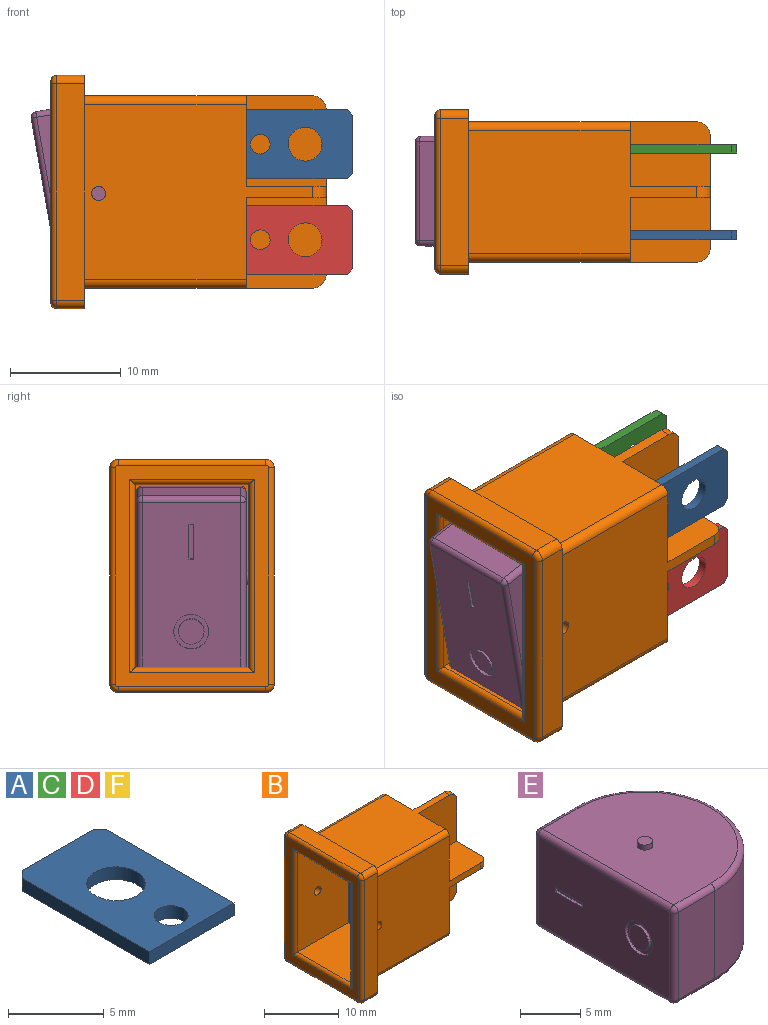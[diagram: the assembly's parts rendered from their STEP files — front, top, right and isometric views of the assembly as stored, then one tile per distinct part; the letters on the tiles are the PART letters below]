
ASSEMBLY  parts=6 mates=5
PART A: 10 faces, bbox 6.2x9.9x0.8 mm
  f0: plane 0.81x0.51mm, normal (0.71,0.7,0), area 0.6mm2, adj f1,f7,f8,f9
  f1: plane 5.25x0.81mm, normal (0,1,0), area 4.3mm2, adj f0,f2,f8,f9
  f2: plane 0.81x0.51mm, normal (-0.71,0.7,0), area 0.6mm2, adj f1,f3,f8,f9
  f3: plane 9.4x0.81mm, normal (-1,0,0), area 7.6mm2, adj f2,f4,f8,f9
  f4: plane 6.25x0.81mm, normal (0,-1,0), area 5.1mm2, adj f3,f7,f8,f9
  f5: cylinder r=1.52mm len=3.05mm, axis (0,0,-1), area 7.8mm2, adj f8,f9
  f6: cylinder r=0.89mm len=1.78mm, axis (0,0,-1), area 4.5mm2, adj f8,f9
  f7: plane 9.4x0.81mm, normal (1,0,0), area 7.6mm2, adj f0,f4,f8,f9
  f8: plane 9.91x6.25mm, normal (0,0,1), area 51.9mm2, adj f0,f1,f2,f3,f4,f5,f6,f7
  f9: plane 9.91x6.25mm, normal (0,0,-1), area 51.9mm2, adj f0,f1,f2,f3,f4,f5,f6,f7
PART B: 74 faces, bbox 24.9x14.9x21.1 mm
  f0: plane 20.07x13.84mm, normal (-1,0,0), area 79.6mm2, adj f58,f59,f60,f61,f62,f63,f64,f65
  f1: plane 8.19x5.84mm, normal (1,0,0), area 42.8mm2, adj f10,f11,f19,f20,f21,f22,f40,f41
  f2: plane 8.19x5.84mm, normal (1,0,0), area 42.8mm2, adj f10,f13,f24,f25,f26,f27,f38,f39
  f3: plane 8.19x5.84mm, normal (1,0,0), area 42.8mm2, adj f12,f13,f29,f30,f31,f32,f36,f37
  f4: plane 8.19x5.84mm, normal (1,0,0), area 42.8mm2, adj f11,f12,f14,f15,f16,f17,f34,f35
  f5: plane 21.08x14.86mm, normal (1,0,0), area 92.3mm2, adj f6,f7,f8,f9,f10,f11,f12,f13
  f6: plane 19.56x2.54mm, normal (0,-1,0), area 49.7mm2, adj f5,f54,f57,f64
  f7: plane 13.34x2.54mm, normal (0,0,-1), area 33.9mm2, adj f5,f54,f55,f63
  f8: plane 19.56x2.54mm, normal (0,1,0), area 49.7mm2, adj f5,f55,f56,f59
  f9: plane 13.34x2.54mm, normal (0,0,1), area 33.9mm2, adj f5,f56,f57,f60
  f10: plane 20.57x15.88mm, normal (0,1,0), area 236.7mm2, adj f1,f2,f5,f39,f40,f48,f50,f53
  f11: plane 20.57x11.18mm, normal (0,0,1), area 169.3mm2, adj f1,f4,f5,f34,f41,f50,f51,f72
  f12: plane 20.57x15.88mm, normal (0,-1,0), area 236.7mm2, adj f3,f4,f5,f35,f36,f49,f51,f52
  f13: plane 20.57x11.18mm, normal (0,0,-1), area 169.3mm2, adj f2,f3,f5,f37,f38,f52,f53,f70
  f14: plane 0.81x0.25mm, normal (0,0,1), area 0.2mm2, adj f4,f15,f17,f18
  f15: plane 6.1x0.25mm, normal (0,-1,0), area 1.5mm2, adj f4,f14,f16,f18
  f16: plane 0.81x0.25mm, normal (0,0,-1), area 0.2mm2, adj f4,f15,f17,f18
  f17: plane 6.1x0.25mm, normal (0,1,0), area 1.5mm2, adj f4,f14,f16,f18
  f18: plane 6.1x0.81mm, normal (1,0,0), area 5mm2, adj f14,f15,f16,f17
  f19: plane 0.81x0.25mm, normal (0,0,1), area 0.2mm2, adj f1,f20,f22,f23
  f20: plane 6.1x0.25mm, normal (0,-1,0), area 1.5mm2, adj f1,f19,f21,f23
  f21: plane 0.81x0.25mm, normal (0,0,-1), area 0.2mm2, adj f1,f20,f22,f23
  f22: plane 6.1x0.25mm, normal (0,1,0), area 1.5mm2, adj f1,f19,f21,f23
  f23: plane 6.1x0.81mm, normal (1,0,0), area 5mm2, adj f19,f20,f21,f22
  f24: plane 0.81x0.25mm, normal (0,0,1), area 0.2mm2, adj f2,f25,f27,f28
  f25: plane 6.1x0.25mm, normal (0,-1,0), area 1.5mm2, adj f2,f24,f26,f28
  f26: plane 0.81x0.25mm, normal (0,0,-1), area 0.2mm2, adj f2,f25,f27,f28
  f27: plane 6.1x0.25mm, normal (0,1,0), area 1.5mm2, adj f2,f24,f26,f28
  f28: plane 6.1x0.81mm, normal (1,0,0), area 5mm2, adj f24,f25,f26,f27
  f29: plane 0.81x0.25mm, normal (0,0,1), area 0.2mm2, adj f3,f30,f32,f33
  f30: plane 6.1x0.25mm, normal (0,-1,0), area 1.5mm2, adj f3,f29,f31,f33
  f31: plane 0.81x0.25mm, normal (0,0,-1), area 0.2mm2, adj f3,f30,f32,f33
  f32: plane 6.1x0.25mm, normal (0,1,0), area 1.5mm2, adj f3,f29,f31,f33
  f33: plane 6.1x0.81mm, normal (1,0,0), area 5mm2, adj f29,f30,f31,f32
  f34: plane 8.19x7.24mm, normal (0,-1,0), area 59mm2, adj f4,f11,f35,f42,f72
  f35: plane 7.24x5.84mm, normal (0,0,1), area 41.9mm2, adj f4,f12,f34,f42,f73
  f36: plane 7.24x5.84mm, normal (0,0,-1), area 41.9mm2, adj f3,f12,f37,f42,f73
  f37: plane 8.19x7.24mm, normal (0,-1,0), area 59mm2, adj f3,f13,f36,f42,f70
  f38: plane 8.19x7.24mm, normal (0,1,0), area 59mm2, adj f2,f13,f39,f42,f70
  f39: plane 7.24x5.84mm, normal (0,0,-1), area 41.9mm2, adj f2,f10,f38,f42,f71
  f40: plane 7.24x5.84mm, normal (0,0,1), area 41.9mm2, adj f1,f10,f41,f42,f71
  f41: plane 8.19x7.24mm, normal (0,1,0), area 59mm2, adj f1,f11,f40,f42,f72
  f42: plane 14.86x10.16mm, normal (1,0,0), area 24.4mm2, adj f34,f35,f36,f37,f38,f39,f40,f41
  f43: plane 16.51x9.65mm, normal (0,1,0), area 158.1mm2, adj f44,f46,f47,f49,f66
  f44: plane 10.29x9.65mm, normal (0,0,-1), area 99.3mm2, adj f43,f45,f47,f67
  f45: plane 16.51x9.65mm, normal (0,-1,0), area 158.1mm2, adj f44,f46,f47,f48,f69
  f46: plane 10.29x9.65mm, normal (0,0,1), area 99.3mm2, adj f43,f45,f47,f68
  f47: plane 16.51x10.29mm, normal (-1,0,0), area 169.8mm2, adj f43,f44,f45,f46
  f48: cylinder r=0.64mm len=1.27mm, axis (0,1,0), area 4.8mm2, adj f10,f45
  f49: cylinder r=0.64mm len=1.27mm, axis (0,1,0), area 4.8mm2, adj f12,f43
  f50: cylinder r=0.76mm len=14.61mm, axis (1,0,0), area 17.5mm2, adj f1,f5,f10,f11
  f51: cylinder r=0.76mm len=14.61mm, axis (-1,0,0), area 17.5mm2, adj f4,f5,f11,f12
  f52: cylinder r=0.76mm len=14.61mm, axis (1,0,0), area 17.5mm2, adj f3,f5,f12,f13
  f53: cylinder r=0.76mm len=14.61mm, axis (-1,0,0), area 17.5mm2, adj f2,f5,f10,f13
  f54: cylinder r=0.76mm len=2.54mm, axis (1,0,0), area 3mm2, adj f5,f6,f7,f65
  f55: cylinder r=0.76mm len=2.54mm, axis (-1,0,0), area 3mm2, adj f5,f7,f8,f61
  f56: cylinder r=0.76mm len=2.54mm, axis (1,0,0), area 3mm2, adj f5,f8,f9,f58
  f57: cylinder r=0.76mm len=2.54mm, axis (-1,0,0), area 3mm2, adj f5,f6,f9,f62
  f58: torus R=0.25mm, axis (1,0,0), area 0.7mm2, adj f0,f56,f59,f60
  f59: cylinder r=0.51mm len=19.56mm, axis (0,0,1), area 15.6mm2, adj f0,f8,f58,f61
  f60: cylinder r=0.51mm len=13.34mm, axis (0,-1,0), area 10.6mm2, adj f0,f9,f58,f62
  f61: torus R=0.25mm, axis (1,0,0), area 0.7mm2, adj f0,f55,f59,f63
  f62: torus R=0.25mm, axis (1,0,0), area 0.7mm2, adj f0,f57,f60,f64
  f63: cylinder r=0.51mm len=13.34mm, axis (0,1,0), area 10.6mm2, adj f0,f7,f61,f65
  f64: cylinder r=0.51mm len=19.56mm, axis (0,0,-1), area 15.6mm2, adj f0,f6,f62,f65
  f65: torus R=0.25mm, axis (1,0,0), area 0.7mm2, adj f0,f54,f63,f64
  f66: cylinder r=0.51mm len=17.53mm, axis (0,0,1), area 13.5mm2, adj f0,f43,f67,f68
  f67: cylinder r=0.51mm len=11.3mm, axis (0,1,0), area 8.5mm2, adj f0,f44,f66,f69
  f68: cylinder r=0.51mm len=11.3mm, axis (0,-1,0), area 8.5mm2, adj f0,f46,f66,f69
  f69: cylinder r=0.51mm len=17.53mm, axis (0,0,-1), area 13.5mm2, adj f0,f45,f67,f68
  f70: cylinder r=1.27mm len=1.27mm, axis (0,-1,0), area 2mm2, adj f13,f37,f38,f42
  f71: cylinder r=1.27mm len=1.27mm, axis (0,0,-1), area 2mm2, adj f10,f39,f40,f42
  f72: cylinder r=1.27mm len=1.27mm, axis (0,1,0), area 2mm2, adj f11,f34,f41,f42
  f73: cylinder r=1.27mm len=1.27mm, axis (0,0,1), area 2mm2, adj f12,f35,f36,f42
PART C: same geometry as A
PART D: same geometry as A
PART E: 33 faces, bbox 13.8x17.9x10.9 mm
  f0: plane 15.49x8.89mm, normal (-1,0,0), area 128.5mm2, adj f11,f14,f15,f16,f17,f22,f24,f27
  f1: cylinder r=8.26mm len=16.51mm, axis (0,0,-1), area 230.6mm2, adj f2,f3,f20,f31
  f2: plane 8.89x4.32mm, normal (0,1,0), area 38.4mm2, adj f1,f19,f24,f29
  f3: plane 8.89x4.32mm, normal (0,-1,0), area 38.4mm2, adj f1,f23,f28,f32
  f4: plane 15.49x12.07mm, normal (0,0,1), area 159.9mm2, adj f6,f19,f20,f22,f23
  f5: plane 15.49x12.07mm, normal (0,0,-1), area 159.9mm2, adj f8,f27,f29,f31,f32
  f6: cylinder r=0.64mm len=1.27mm, axis (0,0,-1), area 2mm2, adj f4,f7
  f7: plane 1.27x1.27mm, normal (0,0,1), area 1.3mm2, adj f6
  f8: cylinder r=0.64mm len=1.27mm, axis (0,0,1), area 2mm2, adj f5,f9
  f9: plane 1.27x1.27mm, normal (0,0,-1), area 1.3mm2, adj f8
  f10: cylinder r=1.16mm len=2.31mm, axis (-1,0,0), area 1.8mm2, adj f12,f13
  f11: cylinder r=1.59mm len=3.18mm, axis (-1,0,0), area 2.5mm2, adj f0,f12
  f12: plane 3.18x3.18mm, normal (-1,0,0), area 3.7mm2, adj f10,f11
  f13: plane 2.31x2.31mm, normal (-1,0,0), area 4.2mm2, adj f10
  f14: plane 3.18x0.25mm, normal (0,0,-1), area 0.8mm2, adj f0,f15,f17,f18
  f15: plane 0.43x0.25mm, normal (0,-1,0), area 0.1mm2, adj f0,f14,f16,f18
  f16: plane 3.18x0.25mm, normal (0,0,1), area 0.8mm2, adj f0,f15,f17,f18
  f17: plane 0.43x0.25mm, normal (0,1,0), area 0.1mm2, adj f0,f14,f16,f18
  f18: plane 3.18x0.43mm, normal (-1,0,0), area 1.4mm2, adj f14,f15,f16,f17
  f19: cylinder r=0.51mm len=4.32mm, axis (1,0,0), area 3.4mm2, adj f2,f4,f20,f21
  f20: torus R=7.75mm, axis (0,0,1), area 20.2mm2, adj f1,f4,f19,f23
  f21: sphere r=0.51mm, area 0.4mm2, adj f19,f22,f24
  f22: cylinder r=0.51mm len=15.49mm, axis (0,1,0), area 12.4mm2, adj f0,f4,f21,f25
  f23: cylinder r=0.51mm len=4.32mm, axis (-1,0,0), area 3.4mm2, adj f3,f4,f20,f25
  f24: cylinder r=0.51mm len=8.89mm, axis (0,0,-1), area 7.1mm2, adj f0,f2,f21,f26
  f25: sphere r=0.51mm, area 0.4mm2, adj f22,f23,f28
  f26: sphere r=0.51mm, area 0.4mm2, adj f24,f27,f29
  f27: cylinder r=0.51mm len=15.49mm, axis (0,-1,0), area 12.4mm2, adj f0,f5,f26,f30
  f28: cylinder r=0.51mm len=8.89mm, axis (0,0,-1), area 7.1mm2, adj f0,f3,f25,f30
  f29: cylinder r=0.51mm len=4.32mm, axis (-1,0,0), area 3.4mm2, adj f2,f5,f26,f31
  f30: sphere r=0.51mm, area 0.4mm2, adj f27,f28,f32
  f31: torus R=7.75mm, axis (0,0,1), area 20.2mm2, adj f1,f5,f29,f32
  f32: cylinder r=0.51mm len=4.32mm, axis (1,0,0), area 3.4mm2, adj f3,f5,f30,f31
PART F: same geometry as A
PLACE A rot(axis=(0.58,0.58,-0.58),120deg) t=(18.92,-1.07,46.87)mm
PLACE B t=(-38.9,98.83,-38.91)mm fixed
PLACE C rot(axis=(0.58,0.58,-0.58),120deg) t=(18.92,6.75,46.87)mm
PLACE D rot(axis=(0.58,0.58,-0.58),120deg) t=(18.92,-1.07,38.23)mm
PLACE E rot(axis=(0.99,-0.09,0.09),90.4deg) t=(-2.2,5.37,-55.11)mm
PLACE F rot(axis=(0.58,0.58,-0.58),120deg) t=(18.92,6.75,38.23)mm
MATE fastened D.f4 <-> B.f33  axis (-1,0,0) through (-21.5,-3.56,12.29)mm
MATE fastened B.f18 <-> A.f4  axis (1,0,0) through (-21.5,-3.56,20.93)mm
MATE fastened F.f4 <-> B.f28  axis (-1,0,0) through (-21.5,4.26,12.29)mm
MATE fastened B.f23 <-> C.f4  axis (1,0,0) through (-21.5,4.26,20.93)mm
MATE revolute E.f1 <-> B.f48  axis (0,-1,0) through (-34.59,-5.04,16.49)mm
